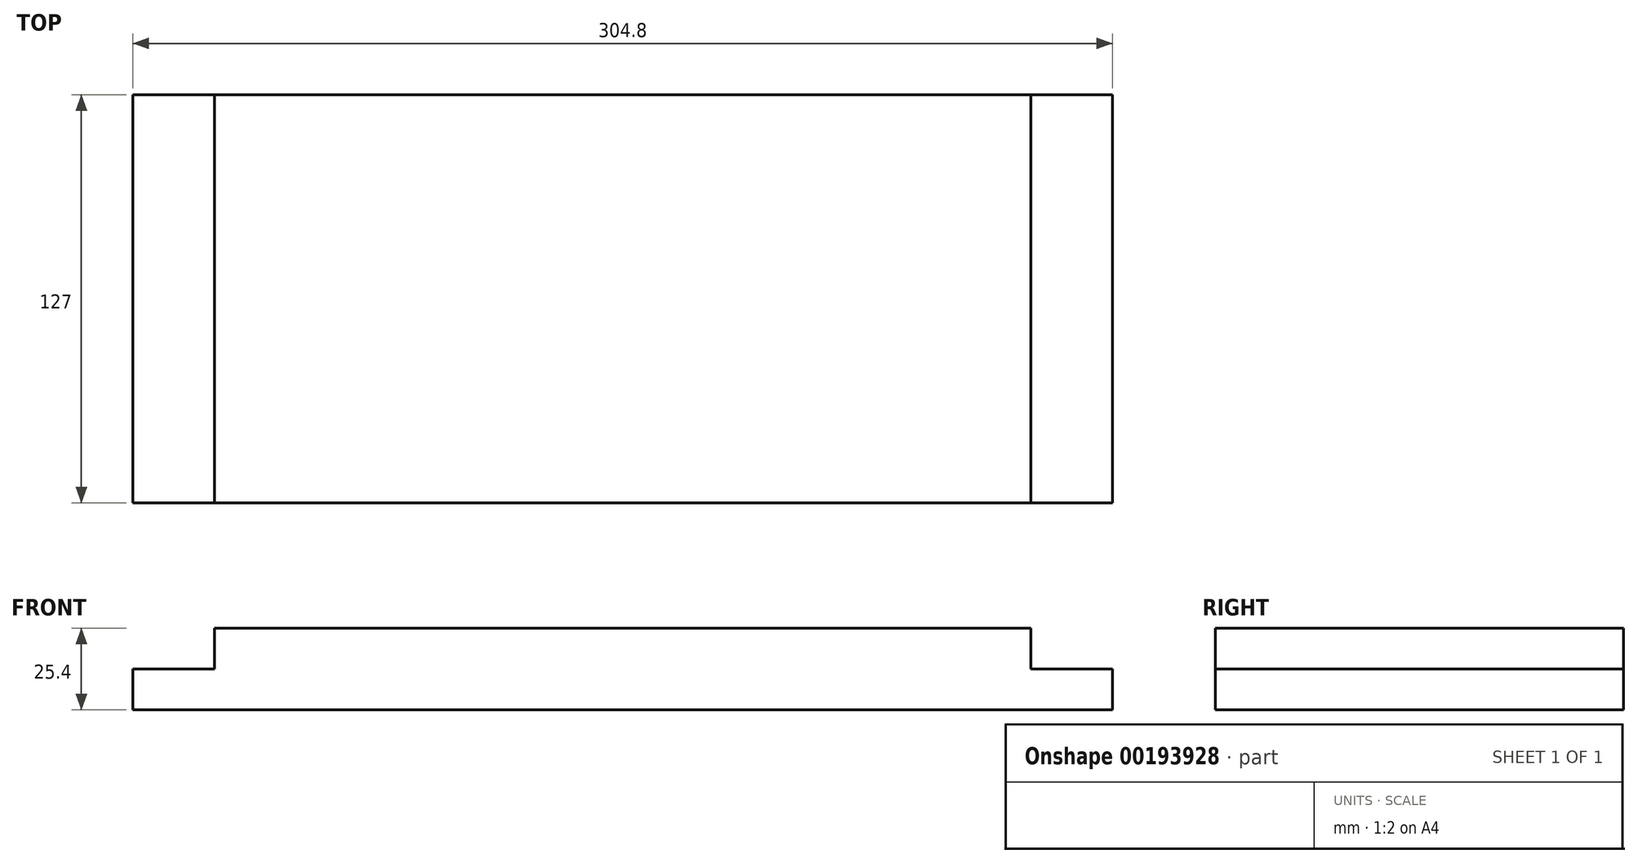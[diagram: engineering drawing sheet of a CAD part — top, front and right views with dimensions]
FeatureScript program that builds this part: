
annotation { "Feature Type Name" : "Feature", "Feature Type Description" : "" }
export const myFeature = defineFeature(function(context is Context, id is Id, definition is map)
    precondition{}
    {
        {
            var Q0;
            Q0=qCreatedBy(makeId("Top.planeOp"),FACE);
            var sketch = newSketch(context, id + "F0", { "sketchPlane" : qUnion([Q0])});
            skLineSegment(sketch, "E0.bottom", {"start": v(-154.88, 25.38) * mm, "end": v(149.92, 25.38) * mm});
            skLineSegment(sketch, "E0.top", {"start": v(-154.88, -127.02) * mm, "end": v(149.92, -127.02) * mm});
            skLineSegment(sketch, "E0.left", {"start": v(-154.88, 25.38) * mm, "end": v(-154.88, -127.02) * mm});
            skLineSegment(sketch, "E0.right", {"start": v(149.92, 25.38) * mm, "end": v(149.92, -127.02) * mm});
            skLineSegment(sketch, "E1.0", {"start": v(-129.48, 25.38) * mm, "end": v(-129.48, -127.02) * mm});
            skLineSegment(sketch, "E2.0", {"start": v(124.52, 25.38) * mm, "end": v(124.52, -127.02) * mm});
            skLineSegment(sketch, "E3.0", {"start": v(-154.88, -114.32) * mm, "end": v(149.92, -114.32) * mm});
            skLineSegment(sketch, "E4.0", {"start": v(-154.88, 12.68) * mm, "end": v(149.92, 12.68) * mm});
            skSolve(sketch);
        }
        {
            var Q0;
            {var subQ0=sQuery(id+"F0.wireOp",EDGE,"E1.0");Q0=makeQuery(id+"F0.imprint","IMPRINT",FACE,{"disambiguationData":[TD([[makeQuery(id+"F0.imprint","IMPRINT",EDGE,{"derivedFrom":subQ0}),1.0]])]});}
            extrude(context, id + "F1", {"entities" : qUnion([Q0]), "depth" : 25.4 * mm});
        }
        {
            var Q0;
            Q0 = qSketchRegion(id + "F0", true);
            extrude(context, id + "F2", {"entities" : qUnion([Q0]), "operationType" : NewBodyOperationType.ADD, "depth" : 12.7 * mm});
        }
        {
            var Q0;
            {var subQ0=sQuery(id+"F0.wireOp",EDGE,"E2.0");var subQ1=sQuery(id+"F0.wireOp",EDGE,"E1.0");var subQ2=sQuery(id+"F0.wireOp",EDGE,"E0.top");var subQ3=sQuery(id+"F0.wireOp",EDGE,"E0.bottom");Q0=makeQuery(id+"F2.boolean.opBoolean","MERGE",FACE,{"derivedFrom":[makeQuery(id+"F1.opExtrude","CAP_FACE",FACE,{"disambiguationData":[OSD([subQ3,subQ2,subQ1,subQ0])],"isStart":true}),makeQuery(id+"F2.opExtrude","CAP_FACE",FACE,{"disambiguationData":[OSD([subQ3,subQ2,sQuery(id+"F0.wireOp",EDGE,"E0.left"),sQuery(id+"F0.wireOp",EDGE,"E0.right"),subQ1,subQ0,sQuery(id+"F0.wireOp",EDGE,"E3.0"),sQuery(id+"F0.wireOp",EDGE,"E4.0")])],"isStart":true})]});}
            var sketch = newSketch(context, id + "F3", { "sketchPlane" : qUnion([Q0])});
            skLineSegment(sketch, "E5.0", {"start": v(-154.88, 114.32) * mm, "end": v(149.92, 114.32) * mm});
            skLineSegment(sketch, "E6.0", {"start": v(-154.88, -12.68) * mm, "end": v(149.92, -12.68) * mm});
            skSolve(sketch);
        }
        {
            var Q0;
            {var subQ0=sQuery(id+"F3.wireOp",EDGE,"E5.0");Q0=makeQuery(id+"F3.imprint","IMPRINT",FACE,{"disambiguationData":[TD([[makeQuery(id+"F3.imprint","IMPRINT",EDGE,{"derivedFrom":subQ0}),1.0]])]});}
            var Q1;
            {var subQ0=sQuery(id+"F3.wireOp",EDGE,"E6.0");Q1=makeQuery(id+"F3.imprint","IMPRINT",FACE,{"disambiguationData":[TD([[makeQuery(id+"F3.imprint","IMPRINT",EDGE,{"derivedFrom":subQ0}),-1.0]])]});}
            extrude(context, id + "F4", {"entities" : qUnion([Q0, Q1]), "operationType" : NewBodyOperationType.REMOVE, "oppositeDirection" : true, "depth" : 25.4 * mm});
        }
    });
